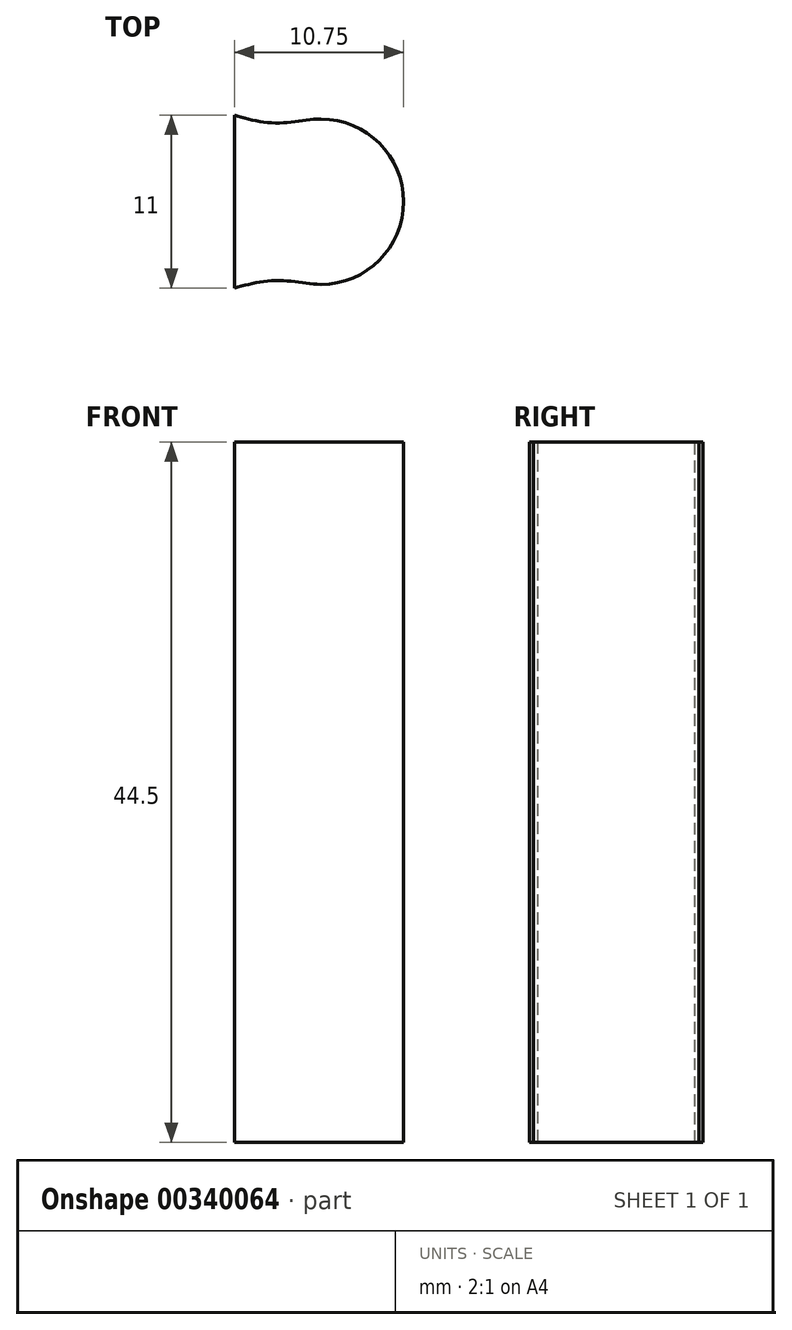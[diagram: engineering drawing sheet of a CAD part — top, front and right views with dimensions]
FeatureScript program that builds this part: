
annotation { "Feature Type Name" : "Feature", "Feature Type Description" : "" }
export const myFeature = defineFeature(function(context is Context, id is Id, definition is map)
    precondition{}
    {
        {
            var Q0;
            Q0=qCreatedBy(makeId("Top.planeOp"),FACE);
            var sketch = newSketch(context, id + "F0", { "sketchPlane" : qUnion([Q0])});
            skLineSegment(sketch, "E0", {"start": v(0, 5.25) * mm, "end": v(0, 0) * mm});
            skLineSegment(sketch, "E1", {"start": v(-5.5, 0) * mm, "end": v(-5.5, 5.5) * mm});
            skLineSegment(sketch, "E2", {"start": v(-5.5, 5.5) * mm, "end": v(-8.58, 5.5) * mm, "construction": true});
            skLineSegment(sketch, "E3", {"start": v(-8.58, 5.5) * mm, "end": v(-8.58, 5) * mm, "construction": true});
            skLineSegment(sketch, "E4", {"start": v(-8.58, 5) * mm, "end": v(7.28, 5) * mm, "construction": true});
            skLineSegment(sketch, "E5", {"start": v(7.95, 0) * mm, "end": v(-7.93, 0) * mm, "construction": true});
            skArc(sketch, "E6.trimOffspring", {"start": v(5.25, 0) * mm, "mid": v(3.71, 3.71) * mm, "end": v(0, 5.25) * mm});
            skPoint(sketch, "E7.start.orphan", {"position": v(-1.6, 5) * mm});
            skLineSegment(sketch, "E8.MirrorCS", {"start": v(-5.5, 0) * mm, "end": v(-5.5, -5.5) * mm});
            skArc(sketch, "E9.MirrorCS", {"start": v(5.25, 0) * mm, "mid": v(3.71, -3.71) * mm, "end": v(0, -5.25) * mm});
            skLineSegment(sketch, "E10", {"start": v(-5.5, 5.3) * mm, "end": v(-2.75, 5.3) * mm, "construction": true});
            skLineSegment(sketch, "E11", {"start": v(-2.75, 5) * mm, "end": v(-2.75, 5.3) * mm, "construction": true});
            skFitSpline(sketch, "E12", {"points": [v(-5.5, 5.5) * mm, v(-2.75, 5) * mm, v(0, 5.25) * mm], "startDerivative": vector(4.88, -1.48) * mm, "endDerivative": vector(5.34, 0) * mm});
            skFitSpline(sketch, "E13.MirrorCS", {"points": [v(-5.5, -5.5) * mm, v(-2.75, -5) * mm, v(0, -5.25) * mm], "startDerivative": vector(4.88, 1.48) * mm, "endDerivative": vector(5.34, 0) * mm});
            skSolve(sketch);
        }
        {
            var Q0;
            Q0=makeQuery(id+"F0.imprint","IMPRINT",FACE,{"disambiguationData":[TD([[makeQuery(id+"F0.imprint","IMPRINT",EDGE,{"derivedFrom":sQuery(id+"F0.wireOp",EDGE,"E1")}),-1.0]])]});
            extrude(context, id + "F1", {"entities" : qUnion([Q0]), "endBound" : BoundingType.SYMMETRIC, "depth" : 44.5 * mm});
        }
    });
